# Revit family: SOL-P
name_source: partatom
category: Lighting Fixtures
revit_build: Autodesk Revit 2018 (Build: 20170223_1515(x64)
units: mm (PartAtom-declared; Revit-internal decimal feet)

## family parameters
Cut with Voids When Loaded = No
Host = Face
Light Source = Yes
Part Type = Normal
Room Calculation Point = Yes
Round Connector Dimension = Use Diameter
Shared = Yes

## types (2) — shared parameters
Color Filter = 16777215
Default Elevation = 4' - 0"
Dimming Lamp Color Temperature Shift = <None>
Emit Shape Visible in Rendering = Yes
Emit from Rectangle Width = 0' - 2"
Fixture Symbol Visiblity = Yes
Fixture Width = 0' - 2 1/4"
Lamp = LED
Photometric Web File = SOL-L-28-HO-4-40K-8.ies
Switch Leg Visibility = No
Tilt Angle = 90.00°

## per-type parameters (varying)
| type | Apparent Load | Emit from Rectangle Length | Fixture Length | Voltage |
| 4' Direct/ Indirect | 41 VA | 4' - 0" | 4' - 0" | 0 V |
| 8' Direct/ Indirect | 81 VA | 8' - 0" | 8' - 0" | 120 V |

## geometry (parser evidence)
native form markers: Sweep x5
no freeform markers — native parametric forms only
